# Revit family: rba-bim-B43949
name_source: partatom
category: Specialty Equipment
revit_build: Autodesk Revit 2018 (Build: 20170223_1515(x64)
units: mm (PartAtom-declared; Revit-internal decimal feet)

## family parameters
Always vertical = Yes
Cut with Voids When Loaded = No
OmniClass Number = 23.40.20.21.34
OmniClass Title = Soap Holders, Dispensers
Part Type = Normal
Room Calculation Point = No
Round Connector Dimension = Use Diameter
Shared = Yes
Work Plane-Based = Yes

## types (1)
- B-43949
    ADA Compliant = Yes
    Assembly Code = C1030210
    Default Elevation = 0 mm  [stored 0 ft]
    Description = Surfaced-Mounted Paper Towel Dispenser And Waste Receptacle
    Manufacturer = Bobrick Washroom Equipment
    Materials and Finishes = Stainless Steel Type 304 Satin Finish
    Model = B43949
    Modified Issue = 20200824.01
    URL = www.rba.com.au

note: [stored X ft] marks values corroborated as IEEE doubles in the binary element streams (Revit-internal decimal feet)

## geometry (parser evidence)
native form markers: Blend x4, Sweep x2
no freeform markers — native parametric forms only
